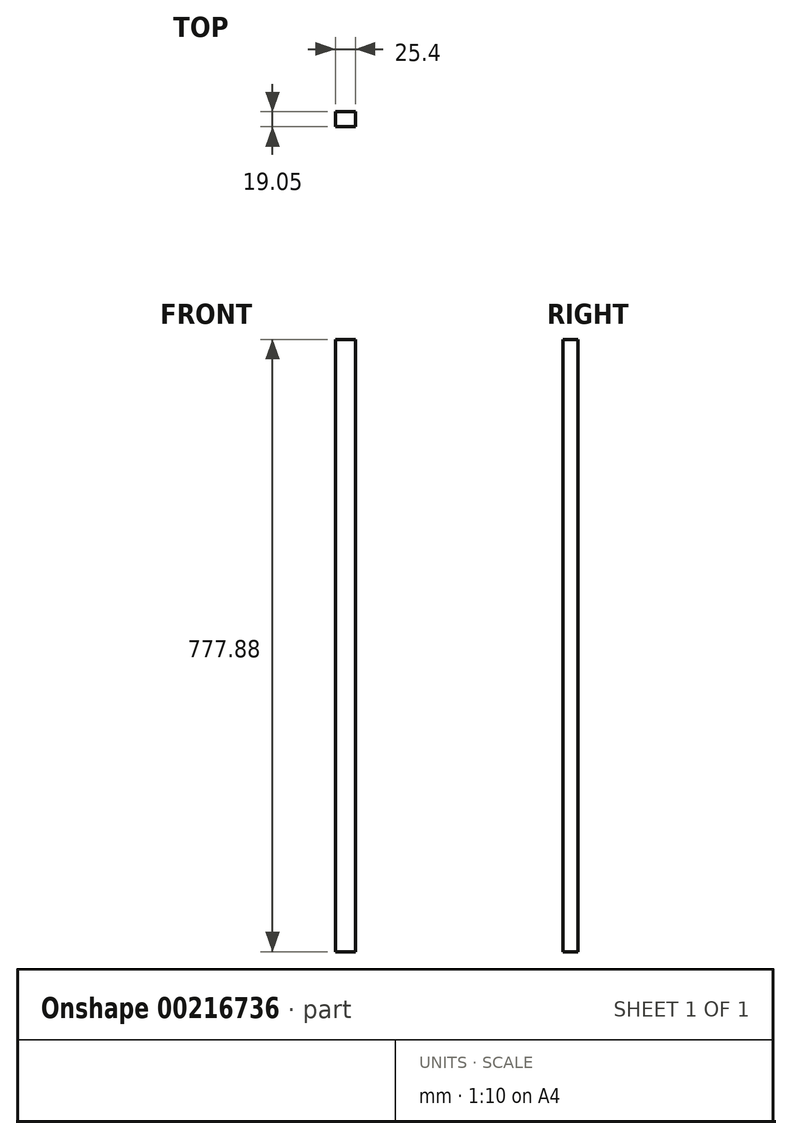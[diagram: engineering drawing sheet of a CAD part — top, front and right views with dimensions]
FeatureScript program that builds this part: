
annotation { "Feature Type Name" : "Feature", "Feature Type Description" : "" }
export const myFeature = defineFeature(function(context is Context, id is Id, definition is map)
    precondition{}
    {
        {
            var Q0;
            Q0=qCreatedBy(makeId("Front.planeOp"),FACE);
            var sketch = newSketch(context, id + "F0", { "sketchPlane" : qUnion([Q0])});
            skLineSegment(sketch, "E0.bottom", {"start": v(0, 0) * mm, "end": v(25.4, 0) * mm});
            skLineSegment(sketch, "E0.top", {"start": v(0, 777.88) * mm, "end": v(25.4, 777.88) * mm});
            skLineSegment(sketch, "E0.left", {"start": v(0, 0) * mm, "end": v(0, 777.88) * mm});
            skLineSegment(sketch, "E0.right", {"start": v(25.4, 0) * mm, "end": v(25.4, 777.88) * mm});
            skSolve(sketch);
        }
        {
            var Q0;
            Q0 = qSketchRegion(id + "F0", true);
            extrude(context, id + "F1", {"entities" : qUnion([Q0]), "depth" : 19.05 * mm});
        }
    });
